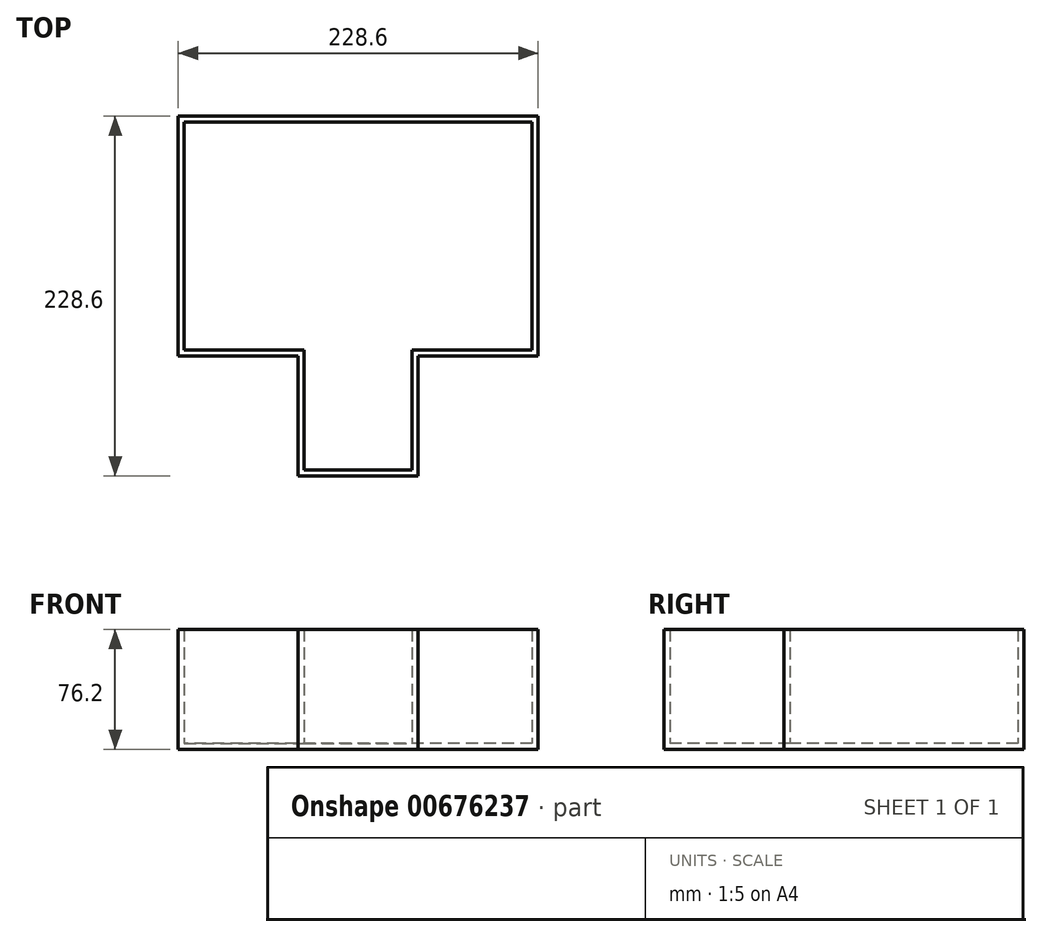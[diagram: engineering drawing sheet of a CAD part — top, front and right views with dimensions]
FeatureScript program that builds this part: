
annotation { "Feature Type Name" : "Feature", "Feature Type Description" : "" }
export const myFeature = defineFeature(function(context is Context, id is Id, definition is map)
    precondition{}
    {
        {
            var Q0;
            Q0=qCreatedBy(makeId("Top.planeOp"),FACE);
            var sketch = newSketch(context, id + "F0", { "sketchPlane" : qUnion([Q0])});
            skLineSegment(sketch, "E0", {"start": v(0, 152.4) * mm, "end": v(-114.3, 152.4) * mm});
            skLineSegment(sketch, "E1", {"start": v(-114.3, 152.4) * mm, "end": v(-114.3, 0) * mm});
            skLineSegment(sketch, "E2", {"start": v(-114.3, 0) * mm, "end": v(-38.1, 0) * mm});
            skLineSegment(sketch, "E3", {"start": v(-38.1, 0) * mm, "end": v(-38.1, -76.2) * mm});
            skLineSegment(sketch, "E4", {"start": v(-38.1, -76.2) * mm, "end": v(0, -76.2) * mm});
            skLineSegment(sketch, "E5", {"start": v(0, 152.4) * mm, "end": v(0, -76.2) * mm});
            skLineSegment(sketch, "E6.MirrorCS", {"start": v(0, 152.4) * mm, "end": v(114.3, 152.4) * mm});
            skLineSegment(sketch, "E7.MirrorCS", {"start": v(114.3, 152.4) * mm, "end": v(114.3, 0) * mm});
            skLineSegment(sketch, "E8.MirrorCS", {"start": v(114.3, 0) * mm, "end": v(38.1, 0) * mm});
            skLineSegment(sketch, "E9.MirrorCS", {"start": v(38.1, 0) * mm, "end": v(38.1, -76.2) * mm});
            skLineSegment(sketch, "E10.MirrorCS", {"start": v(38.1, -76.2) * mm, "end": v(0, -76.2) * mm});
            skLineSegment(sketch, "E11", {"start": v(0, 152.4) * mm, "end": v(0, 148.6) * mm});
            skLineSegment(sketch, "E12", {"start": v(0, 148.6) * mm, "end": v(-110.5, 148.6) * mm});
            skLineSegment(sketch, "E13", {"start": v(-110.5, 148.6) * mm, "end": v(-110.49, 3.81) * mm});
            skLineSegment(sketch, "E14", {"start": v(-110.49, 3.81) * mm, "end": v(-34.29, 3.81) * mm});
            skLineSegment(sketch, "E15", {"start": v(-34.29, 3.81) * mm, "end": v(-34.29, -72.39) * mm});
            skLineSegment(sketch, "E16", {"start": v(-34.29, -72.39) * mm, "end": v(0, -72.39) * mm});
            skLineSegment(sketch, "E17.MirrorCS", {"start": v(0, 148.6) * mm, "end": v(110.5, 148.6) * mm});
            skLineSegment(sketch, "E18.MirrorCS", {"start": v(110.5, 148.6) * mm, "end": v(110.49, 3.81) * mm});
            skLineSegment(sketch, "E19.MirrorCS", {"start": v(110.49, 3.81) * mm, "end": v(34.29, 3.81) * mm});
            skLineSegment(sketch, "E20.MirrorCS", {"start": v(34.29, 3.81) * mm, "end": v(34.29, -72.39) * mm});
            skLineSegment(sketch, "E21.MirrorCS", {"start": v(34.29, -72.39) * mm, "end": v(0, -72.39) * mm});
            skSolve(sketch);
        }
        {
            var Q0;
            {var subQ0=sQuery(id+"F0.wireOp",EDGE,"E12");Q0=makeQuery(id+"F0.imprint","IMPRINT",FACE,{"disambiguationData":[TD([[makeQuery(id+"F0.imprint","IMPRINT",EDGE,{"derivedFrom":subQ0}),1.0]])]});}
            var Q1;
            {var subQ0=sQuery(id+"F0.wireOp",EDGE,"E17.MirrorCS");Q1=makeQuery(id+"F0.imprint","IMPRINT",FACE,{"disambiguationData":[TD([[makeQuery(id+"F0.imprint","IMPRINT",EDGE,{"derivedFrom":subQ0}),-1.0]])]});}
            extrude(context, id + "F1", {"entities" : qUnion([Q0, Q1]), "depth" : 3.8 * mm, "offsetDistance" : 25.4 * mm});
        }
        {
            var Q0;
            Q0=makeQuery(id+"F0.imprint","IMPRINT",FACE,{"disambiguationData":[TD([[makeQuery(id+"F0.imprint","IMPRINT",EDGE,{"derivedFrom":sQuery(id+"F0.wireOp",EDGE,"E6.MirrorCS")}),-1.0]])]});
            var Q1;
            Q1=makeQuery(id+"F0.imprint","IMPRINT",FACE,{"disambiguationData":[TD([[makeQuery(id+"F0.imprint","IMPRINT",EDGE,{"derivedFrom":sQuery(id+"F0.wireOp",EDGE,"E0")}),1.0]])]});
            extrude(context, id + "F2", {"entities" : qUnion([Q0, Q1]), "operationType" : NewBodyOperationType.ADD, "depth" : 76.2 * mm, "offsetDistance" : 25.4 * mm});
        }
    });
